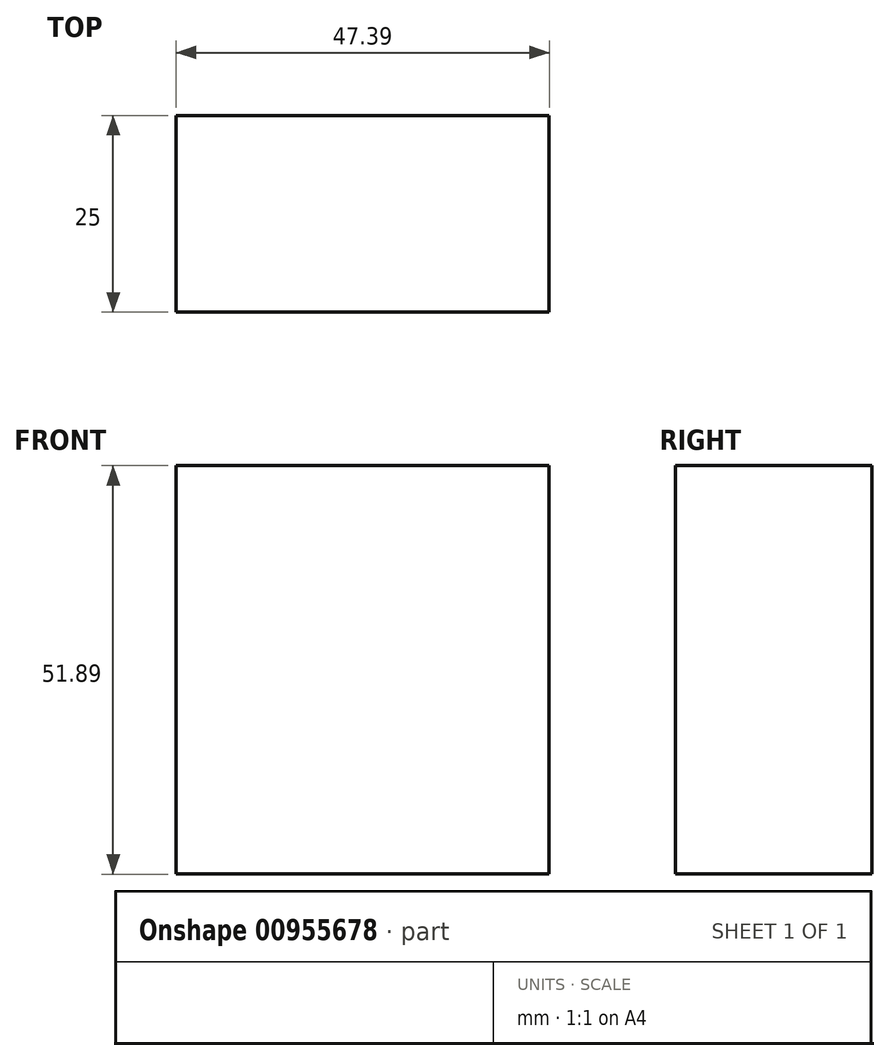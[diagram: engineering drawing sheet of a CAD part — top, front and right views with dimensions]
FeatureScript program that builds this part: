
annotation { "Feature Type Name" : "Feature", "Feature Type Description" : "" }
export const myFeature = defineFeature(function(context is Context, id is Id, definition is map)
    precondition{}
    {
        {
            var Q0;
            Q0=qCreatedBy(makeId("Front.planeOp"),FACE);
            var sketch = newSketch(context, id + "F0", { "sketchPlane" : qUnion([Q0])});
            skLineSegment(sketch, "E0.bottom", {"start": v(-123.17, 19.46) * mm, "end": v(-75.78, 19.46) * mm});
            skLineSegment(sketch, "E0.top", {"start": v(-123.17, -32.43) * mm, "end": v(-75.78, -32.43) * mm});
            skLineSegment(sketch, "E0.left", {"start": v(-123.17, 19.46) * mm, "end": v(-123.17, -32.43) * mm});
            skLineSegment(sketch, "E0.right", {"start": v(-75.78, 19.46) * mm, "end": v(-75.78, -32.43) * mm});
            skSolve(sketch);
        }
        {
            var Q0;
            Q0 = qSketchRegion(id + "F0", true);
            extrude(context, id + "F1", {"entities" : qUnion([Q0]), "depth" : 25 * mm, "offsetDistance" : 25 * mm});
        }
    });
